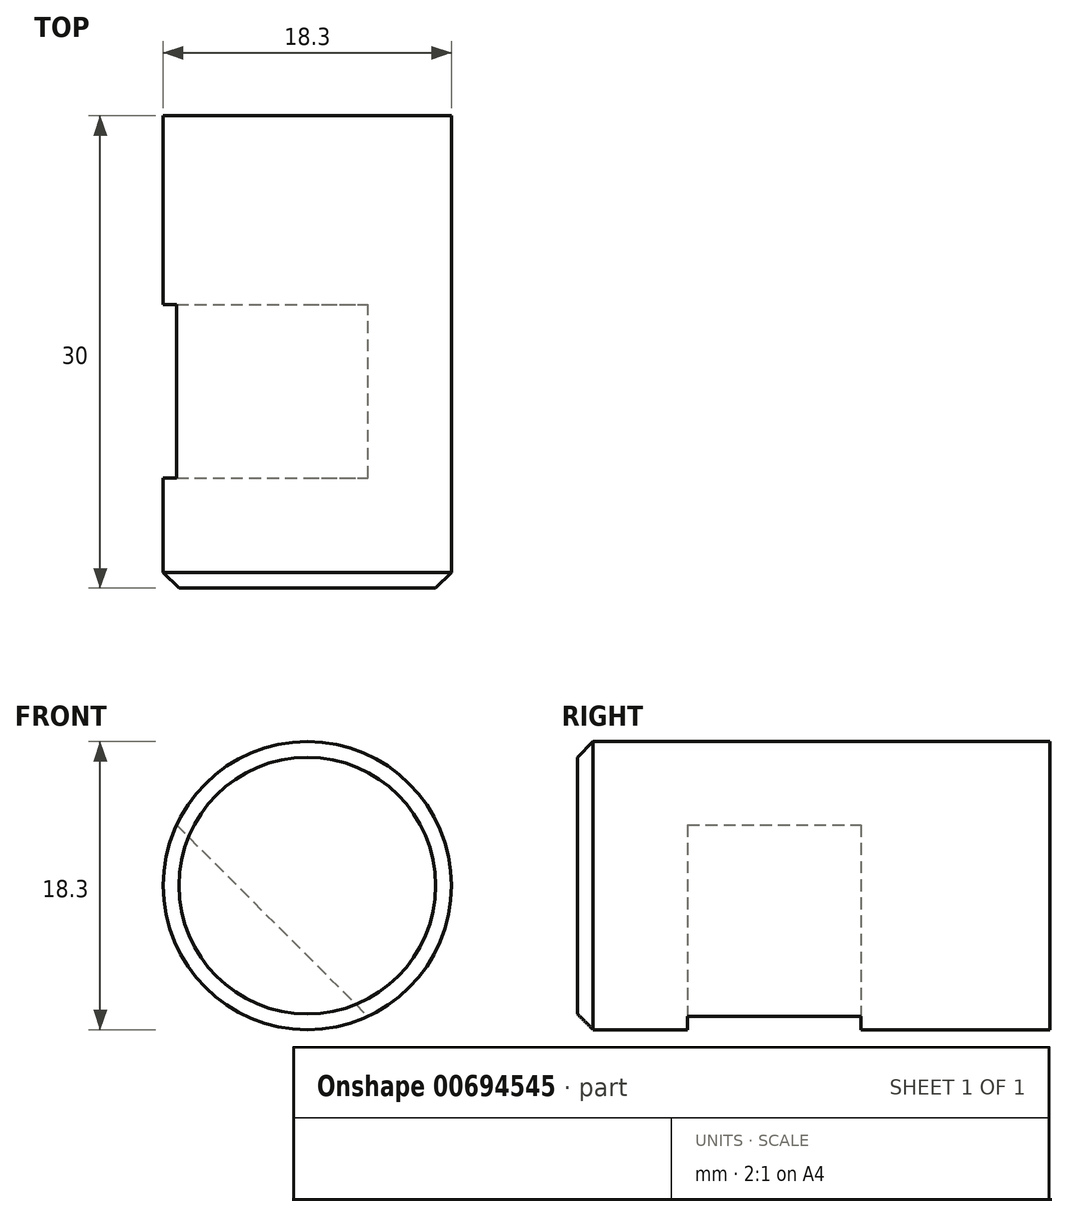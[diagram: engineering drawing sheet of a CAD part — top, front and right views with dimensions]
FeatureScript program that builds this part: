
annotation { "Feature Type Name" : "Feature", "Feature Type Description" : "" }
export const myFeature = defineFeature(function(context is Context, id is Id, definition is map)
    precondition{}
    {
        {
            var Q0;
            Q0=qCreatedBy(makeId("Front.planeOp"),FACE);
            var sketch = newSketch(context, id + "F0", { "sketchPlane" : qUnion([Q0])});
            skCircle(sketch, "E0", {"center": v(0, 0) * mm, "radius": 9.15 * mm});
            skSolve(sketch);
        }
        {
            var Q0;
            Q0 = qSketchRegion(id + "F0", true);
            extrude(context, id + "F1", {"entities" : qUnion([Q0]), "depth" : 30 * mm, "offsetDistance" : 25 * mm});
        }
        {
            var Q0;
            Q0=makeQuery(id+"F1.opExtrude","CAP_EDGE",EDGE,{"disambiguationData":[OSD([sQuery(id+"F0.wireOp",EDGE,"E0")])],"isStart":false});
            chamfer(context, id + "F2", {"entities" : qUnion([Q0]), "chamferType" : ChamferType.OFFSET_ANGLE, "width" : 1 * mm, "oppositeDirection" : false, "angle" : 45 * degree, "tangentPropagation" : true});
        }
        {
            var Q0;
            Q0=qCreatedBy(makeId("Front.planeOp"),FACE);
            cPlane(context, id + "F3", {"entities" : qUnion([Q0]), "cplaneType" : CPlaneType.OFFSET, "offset" : 20 * mm, "width" : 150 * mm, "height" : 150 * mm});
        }
        {
            var Q0;
            Q0=qCreatedBy(id+"F3.planeOp",FACE);
            var sketch = newSketch(context, id + "F4", { "sketchPlane" : qUnion([Q0])});
            skLineSegment(sketch, "E1", {"start": v(-4.45, 0) * mm, "end": v(-8.3, -3.85) * mm});
            skLineSegment(sketch, "E2", {"start": v(-4.45, 0) * mm, "end": v(0, -4.45) * mm});
            skLineSegment(sketch, "E3", {"start": v(0, -4.45) * mm, "end": v(-3.85, -8.3) * mm});
            skArc(sketch, "E4", {"start": v(-8.3, -3.85) * mm, "mid": v(-6.47, -6.47) * mm, "end": v(-3.85, -8.3) * mm});
            skSolve(sketch);
        }
        {
            var Q0;
            Q0 = qSketchRegion(id + "F4", true);
            extrude(context, id + "F5", {"entities" : qUnion([Q0]), "operationType" : NewBodyOperationType.REMOVE, "depth" : 3 * mm, "offsetDistance" : 25 * mm, "hasSecondDirection" : true, "secondDirectionOppositeDirection" : true, "secondDirectionDepth" : 8 * mm});
        }
        {
            var Q0;
            Q0=makeQuery(id+"F5.boolean.opBoolean","COPY",FACE,{"derivedFrom":makeQuery(id+"F5.opExtrude","SWEPT_FACE",FACE,{"disambiguationData":[OSD([sQuery(id+"F4.wireOp",EDGE,"E1")])]})});
            extrude(context, id + "F6", {"entities" : qUnion([Q0]), "operationType" : NewBodyOperationType.REMOVE, "oppositeDirection" : true, "depth" : 25 * mm, "offsetDistance" : 25 * mm, "hasSecondDirection" : true, "secondDirectionOppositeDirection" : false, "secondDirectionDepth" : 25 * mm});
        }
    });
